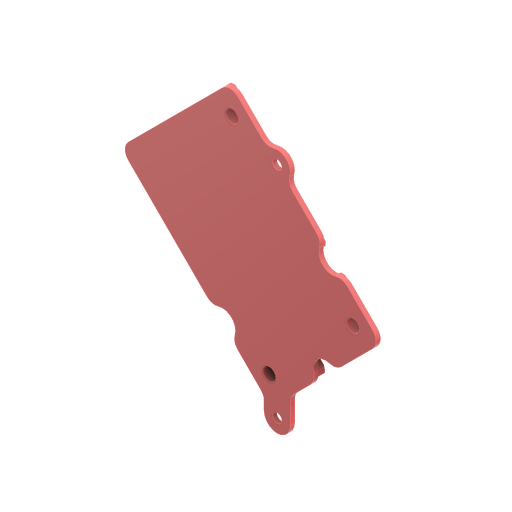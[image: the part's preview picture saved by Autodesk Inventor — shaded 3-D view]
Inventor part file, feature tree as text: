
AUTODESK INVENTOR PART (.ipt)
format: ipt  version: 2023 (Build 270158000, 158)  size: 300,032 bytes
history: native  units: mm
features: sketch x8, extrude x7, fillet x1, projected_geometry x1
ambient origin geometry x8: Origin, YZ Plane, XZ Plane, XY Plane, X Axis, Y Axis, Z Axis, Center Point
bodies: Solid1 (feature_tree)
feature tree (17):
  sketch  "Sketch1"  dims[d1=50.0mm d2=14.644661mm d3=4.0mm d4=4.0mm d5=4.0mm d6=4.0mm d7=3.3mm d8=4.0mm d9=4.0mm d10=4.0mm d11=4.0mm d12=3.3mm d13=25.0mm d14=25.0mm d15=1.0mm]
  extrude  "Extrusion1"  Depth=25.0mm
  extrude  "North Aligner"  Depth=1.0mm
  extrude  "East Aligner"  Depth=1.0mm
  sketch  "Sketch3"  dims[d28=1.0mm d29=70.71mm]
  sketch  "Sketch Driven Pattern1"  dims[d16=1.0mm d17=1.0mm]
  sketch  "Sketch Driven Pattern2"  dims[d18=1.0mm d25=1.0mm]
  extrude  "Extrusion4"  Depth=1.0mm
  extrude  "Extrusion5"  Depth=70.71mm
  sketch  "Sketch6"  dims[d37=3.0mm d38=0.0mm d39=50.0mm d40=50.0mm d41=30.0mm d43=50.0mm d44=20.0mm d46=50.0mm d49=20.0mm d51=50.0mm d52=20.0mm d54=50.0mm d57=78.0mm d59=54.0mm d60=9.533mm d61=97.066mm d62=70.71mm d63=8.355mm d64=6.0mm d65=6.0mm d66=6.0mm d67=6.0mm d68=0.0mm d69=0.0mm d70=12.0mm d71=45.0deg d72=12.0mm d73=0.0mm d74=0.0mm d75=4.4mm d76=25.0mm d77=25.0mm d78=4.4mm d79=75.0mm d80=25.0mm d81=12.0mm d88=12.0mm d89=12.0mm d90=10.0mm d91=0.0mm d92=0.0mm d93=0.0mm d94=5.0mm]
  extrude  "Extrusion6"  Depth=31.355mm
  extrude  "Extrusion7"  Depth=2.0mm TaperAngle=0.0deg
  fillet  "Fillet1"  Radius=3.0mm
  sketch  "Sketch2"  dims[d26=1.0mm d27=1.0mm]
  sketch  "Sketch4"  dims[d30=45.0deg d31=31.355mm]
  projected_geometry  "Projected Loop1"
  sketch  "Sketch5"  dims[d32=65.711mm d33=2.0mm d34=0.0mm d35=3.0mm d36=0.0mm]
